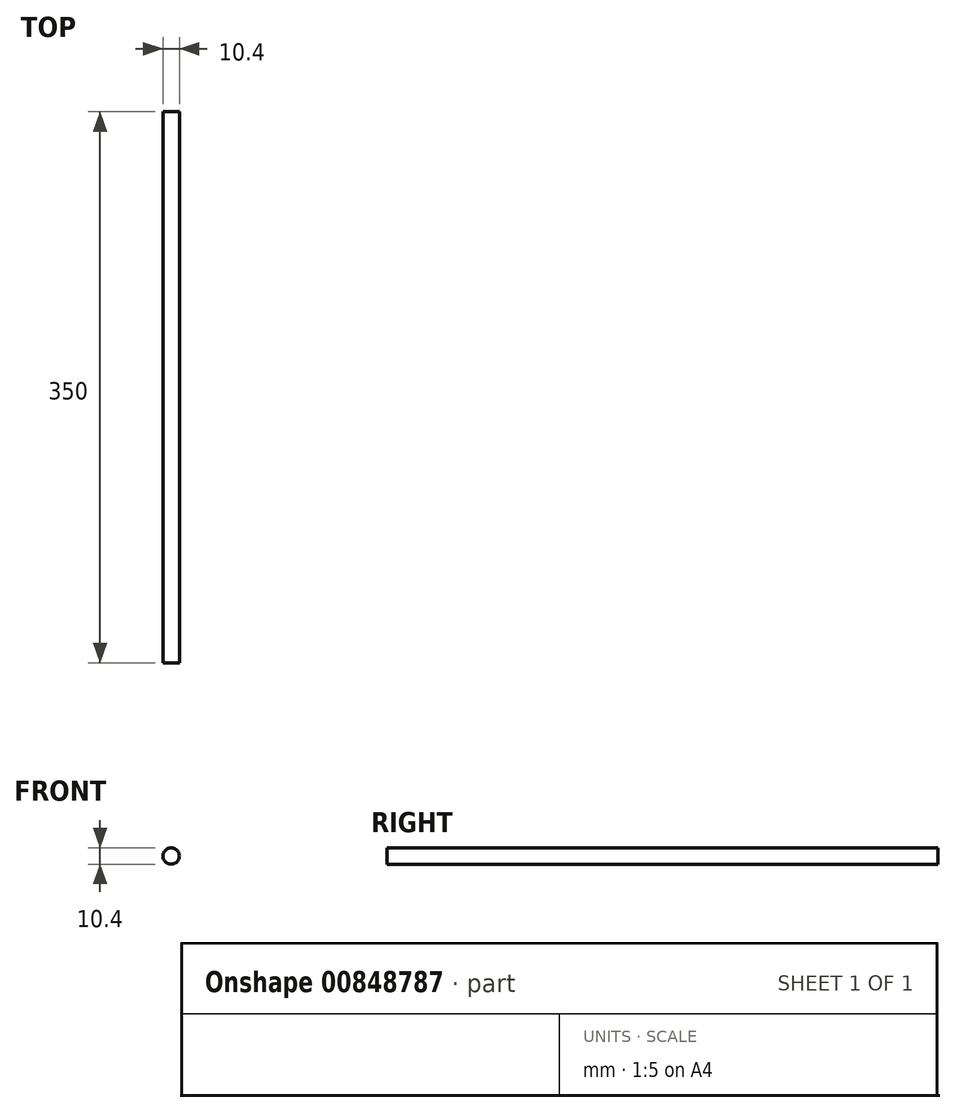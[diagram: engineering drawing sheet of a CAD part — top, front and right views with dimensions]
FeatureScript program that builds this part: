
annotation { "Feature Type Name" : "Feature", "Feature Type Description" : "" }
export const myFeature = defineFeature(function(context is Context, id is Id, definition is map)
    precondition{}
    {
        {
            var Q0;
            Q0=qCreatedBy(makeId("Front.planeOp"),FACE);
            var sketch = newSketch(context, id + "F0", { "sketchPlane" : qUnion([Q0])});
            skCircle(sketch, "E0", {"center": v(0, 0) * mm, "radius": 5.2 * mm});
            skSolve(sketch);
        }
        {
            var Q0;
            Q0=makeQuery(id+"F0.imprint","IMPRINT",FACE,{"disambiguationData":[TD([[makeQuery(id+"F0.imprint","IMPRINT",EDGE,{"derivedFrom":sQuery(id+"F0.wireOp",EDGE,"E0")}),1.0]])]});
            extrude(context, id + "F1", {"entities" : qUnion([Q0]), "depth" : 350 * mm, "offsetDistance" : 25 * mm});
        }
    });
